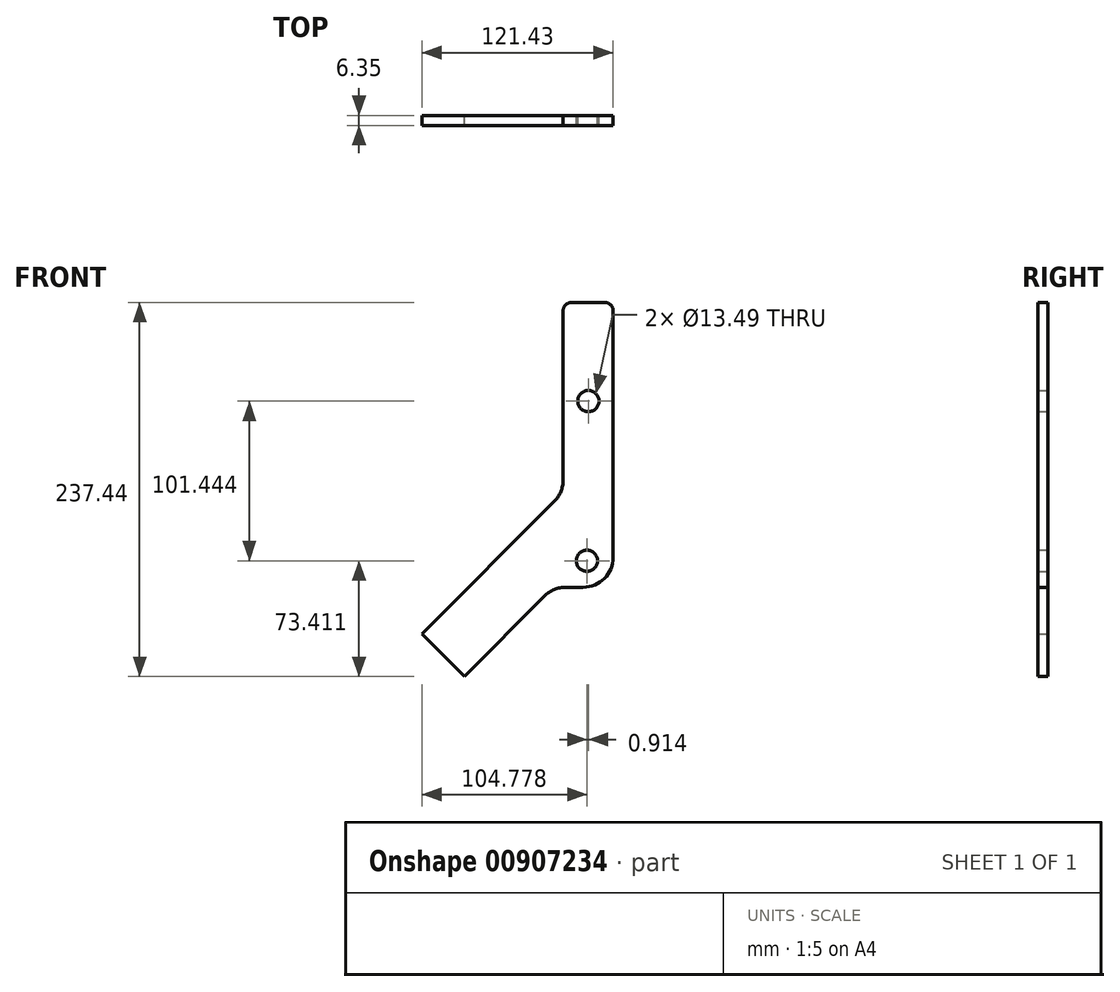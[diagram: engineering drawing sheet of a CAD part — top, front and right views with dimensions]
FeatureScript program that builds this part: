
annotation { "Feature Type Name" : "Feature", "Feature Type Description" : "" }
export const myFeature = defineFeature(function(context is Context, id is Id, definition is map)
    precondition{}
    {
        {
            var Q0;
            Q0=qCreatedBy(makeId("Front.planeOp"),FACE);
            var sketch = newSketch(context, id + "F0", { "sketchPlane" : qUnion([Q0])});
            skLineSegment(sketch, "E0", {"start": v(6.25, 180.83) * mm, "end": v(38, 180.83) * mm});
            skLineSegment(sketch, "E1", {"start": v(38, 180.83) * mm, "end": v(38, 33.02) * mm});
            skLineSegment(sketch, "E2", {"start": v(6.25, 60.22) * mm, "end": v(6.25, 180.83) * mm});
            skLineSegment(sketch, "E3", {"start": v(0, 0) * mm, "end": v(-20.58, -20.64) * mm});
            skLineSegment(sketch, "E4", {"start": v(-20.58, -20.64) * mm, "end": v(-47.56, 6.27) * mm, "construction": true});
            skLineSegment(sketch, "E5", {"start": v(-47.56, 6.27) * mm, "end": v(6.25, 60.22) * mm});
            skLineSegment(sketch, "E6", {"start": v(6.25, 0) * mm, "end": v(38, 0) * mm});
            skLineSegment(sketch, "E7", {"start": v(38, 0) * mm, "end": v(38, 33.02) * mm});
            skLineSegment(sketch, "E8", {"start": v(38, 0) * mm, "end": v(0, 0) * mm});
            skPoint(sketch, "E9.orphan", {"position": v(0, 0) * mm});
            skLineSegment(sketch, "E10", {"start": v(-47.56, 6.27) * mm, "end": v(-83.43, -29.7) * mm});
            skLineSegment(sketch, "E11", {"start": v(-83.43, -29.7) * mm, "end": v(-56.46, -56.6) * mm});
            skLineSegment(sketch, "E12", {"start": v(-56.46, -56.6) * mm, "end": v(-20.58, -20.64) * mm});
            skSolve(sketch);
        }
        {
            var Q0;
            Q0=qSketchRegion(id+"F0",true);
            extrude(context, id + "F1", {"entities" : qUnion([Q0]), "depth" : 6.35 * mm, "offsetDistance" : 25.4 * mm});
        }
        {
            var Q0;
            Q0=makeQuery(id+"F1.opExtrude","CAP_FACE",FACE,{"disambiguationData":[OSD([sQuery(id+"F0.wireOp",EDGE,"E0"),sQuery(id+"F0.wireOp",EDGE,"E1"),sQuery(id+"F0.wireOp",EDGE,"E2"),sQuery(id+"F0.wireOp",EDGE,"E3"),sQuery(id+"F0.wireOp",EDGE,"E4"),sQuery(id+"F0.wireOp",EDGE,"E5"),sQuery(id+"F0.wireOp",EDGE,"gKiY4kpW-ng0u-sDTf-hIyV-E0I1T0kX8aFS")])],"isStart":false});
            var sketch = newSketch(context, id + "F2", { "sketchPlane" : qUnion([Q0])});
            skPoint(sketch, "E13", {"position": v(22.26, 118.24) * mm});
            skPoint(sketch, "E14", {"position": v(21.35, 16.8) * mm});
            skCircle(sketch, "E15", {"center": v(22.26, 118.24) * mm, "radius": 7.2 * mm, "construction": true});
            skCircle(sketch, "E16", {"center": v(21.35, 16.8) * mm, "radius": 7.2 * mm, "construction": true});
            skSolve(sketch);
        }
        {
            var Q0;
            Q0=sQuery(id+"F2.wireOp",VERTEX,"E13");
            var Q1;
            Q1=sQuery(id+"F2.wireOp",VERTEX,"E14");
            var Q2;
            Q2=makeQuery(id+"F1.opExtrude","SWEPT_BODY",BODY,{"disambiguationData":[OSD([sQuery(id+"F0.wireOp",EDGE,"E0"),sQuery(id+"F0.wireOp",EDGE,"E1"),sQuery(id+"F0.wireOp",EDGE,"E2"),sQuery(id+"F0.wireOp",EDGE,"E3"),sQuery(id+"F0.wireOp",EDGE,"E4"),sQuery(id+"F0.wireOp",EDGE,"E5"),sQuery(id+"F0.wireOp",EDGE,"gKiY4kpW-ng0u-sDTf-hIyV-E0I1T0kX8aFS")])]});
            hole(context, id + "F3", {"style" : HoleStyle.SIMPLE, "endStyle" : HoleEndStyle.THROUGH, "standardTappedOrClearance" : lookupTablePath({ "fit" : "Free", "standard" : "ANSI", "size" : "1/2", "type" : "Clearance" }), "standardBlindInLast" : lookupTablePath({ "fit" : "Free", "standard" : "ANSI", "engagement" : "75%", "pitch" : "13 tpi", "size" : "1/2", "type" : "Clearance & tapped" }), "holeDiameter" : 13.5 * mm, "majorDiameter" : 12.7 * mm, "isTappedThrough" : true, "tappedDepth" : 8.47 * mm, "tapClearance" : 3, "locations" : qUnion([Q0, Q1]), "scope" : qUnion([Q2]), "startStyle" : HoleStartStyle.SKETCH});
        }
        {
            var Q0;
            Q0=makeQuery(id+"F1.opExtrude","SWEPT_EDGE",EDGE,{"disambiguationData":[OSD([sQuery(id+"F0.wireOp",EDGE,"E2"),sQuery(id+"F0.wireOp",EDGE,"E5")])]});
            var Q1;
            Q1=makeQuery(id+"F1.opExtrude","SWEPT_EDGE",EDGE,{"disambiguationData":[OSD([sQuery(id+"F0.wireOp",EDGE,"E7"),sQuery(id+"F0.wireOp",EDGE,"E8")])]});
            var Q2;
            Q2=makeQuery(id+"F1.opExtrude","SWEPT_EDGE",EDGE,{"disambiguationData":[OSD([sQuery(id+"F0.wireOp",EDGE,"E3"),sQuery(id+"F0.wireOp",EDGE,"E8")])]});
            fillet(context, id + "F4", {"entities" : qUnion([Q0, Q1, Q2]), "tangentPropagation" : true, "radius" : 19.05 * mm, "defaultsChanged" : false, "vertexSettings" : [], "allowEdgeOverflow" : false});
        }
        {
            var Q0;
            Q0=makeQuery(id+"F1.opExtrude","SWEPT_EDGE",EDGE,{"disambiguationData":[OSD([sQuery(id+"F0.wireOp",EDGE,"E0"),sQuery(id+"F0.wireOp",EDGE,"E2")])]});
            var Q1;
            Q1=makeQuery(id+"F1.opExtrude","SWEPT_EDGE",EDGE,{"disambiguationData":[OSD([sQuery(id+"Fq38At4ci81HlFv_0.wireOp",EDGE,"VVe9A18r-VORx-4CNg-MuIO-dTXUSACqtpxO"),sQuery(id+"F0.wireOp",EDGE,"E0"),sQuery(id+"F0.wireOp",EDGE,"E1")])]});
            fillet(context, id + "F5", {"entities" : qUnion([Q0, Q1]), "tangentPropagation" : true, "radius" : 5.08 * mm, "defaultsChanged" : false, "vertexSettings" : [], "allowEdgeOverflow" : false});
        }
    });
